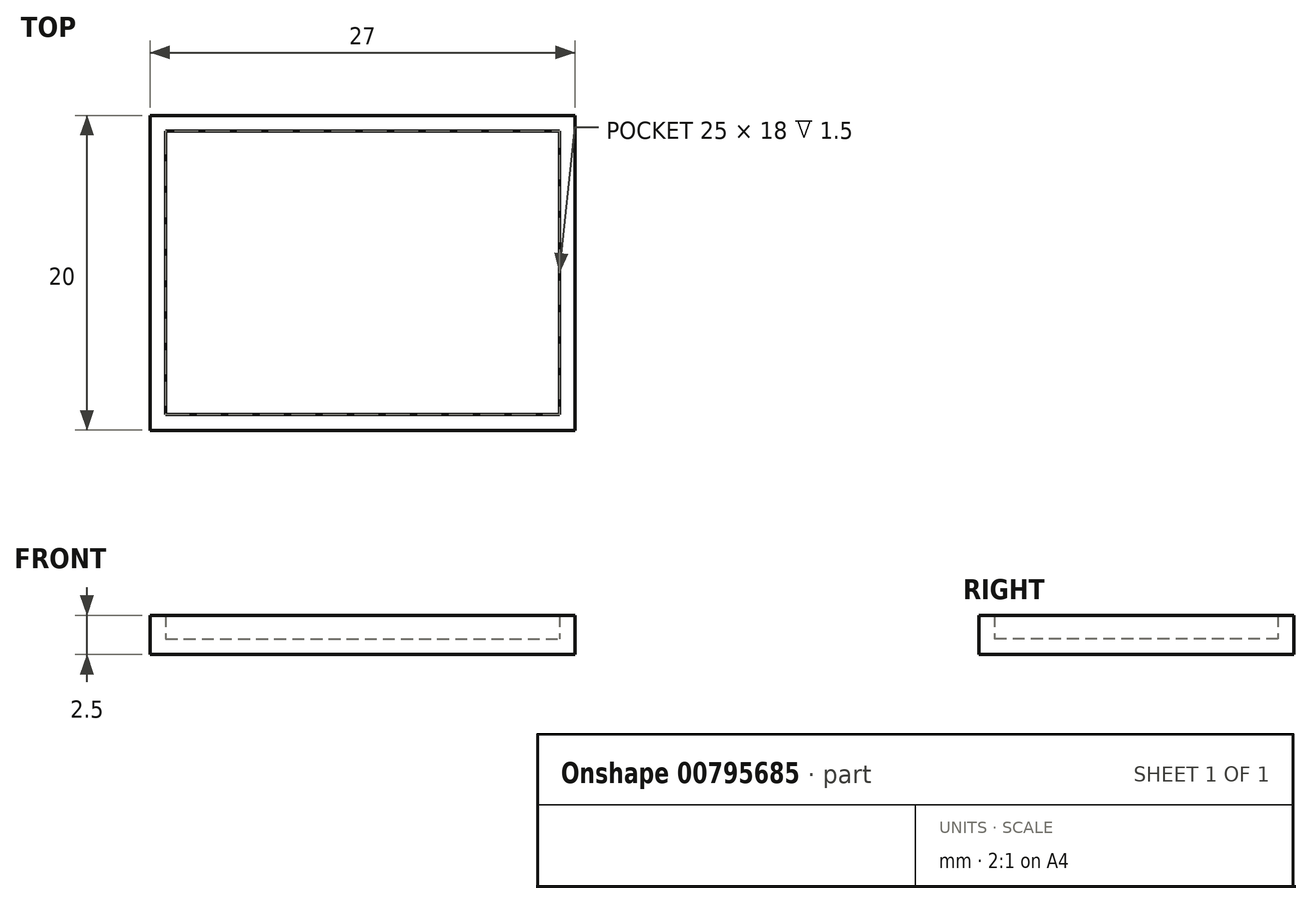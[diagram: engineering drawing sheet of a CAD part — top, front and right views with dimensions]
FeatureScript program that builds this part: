
annotation { "Feature Type Name" : "Feature", "Feature Type Description" : "" }
export const myFeature = defineFeature(function(context is Context, id is Id, definition is map)
    precondition{}
    {
        {
            var Q0;
            Q0=qCreatedBy(makeId("Top.planeOp"),FACE);
            var sketch = newSketch(context, id + "F0", { "sketchPlane" : qUnion([Q0])});
            skLineSegment(sketch, "E0.bottom", {"start": v(-48.16, 20.25) * mm, "end": v(-23.16, 20.25) * mm});
            skLineSegment(sketch, "E0.top", {"start": v(-48.16, 2.25) * mm, "end": v(-23.16, 2.25) * mm});
            skLineSegment(sketch, "E0.left", {"start": v(-48.16, 20.25) * mm, "end": v(-48.16, 2.25) * mm});
            skLineSegment(sketch, "E0.right", {"start": v(-23.16, 20.25) * mm, "end": v(-23.16, 2.25) * mm});
            skLineSegment(sketch, "E1.0", {"start": v(-49.16, 21.25) * mm, "end": v(-22.16, 21.25) * mm});
            skLineSegment(sketch, "E1.1", {"start": v(-49.16, 21.25) * mm, "end": v(-49.16, 1.25) * mm});
            skLineSegment(sketch, "E1.2", {"start": v(-49.16, 1.25) * mm, "end": v(-22.16, 1.25) * mm});
            skLineSegment(sketch, "E1.3", {"start": v(-22.16, 21.25) * mm, "end": v(-22.16, 1.25) * mm});
            skLineSegment(sketch, "E2", {"start": v(-23.16, 20.25) * mm, "end": v(-22.16, 20.25) * mm});
            skLineSegment(sketch, "E3", {"start": v(-23.16, 2.25) * mm, "end": v(-22.16, 2.25) * mm});
            skLineSegment(sketch, "E4", {"start": v(-48.16, 2.25) * mm, "end": v(-49.16, 2.25) * mm});
            skLineSegment(sketch, "E5", {"start": v(-48.16, 20.25) * mm, "end": v(-49.16, 20.25) * mm});
            skSolve(sketch);
        }
        {
            var Q0;
            Q0=makeQuery(id+"F0.imprint","IMPRINT",FACE,{"disambiguationData":[TD([[makeQuery(id+"F0.imprint","IMPRINT",EDGE,{"derivedFrom":sQuery(id+"F0.wireOp",EDGE,"E0.bottom")}),-1.0]])]});
            extrude(context, id + "F1", {"entities" : qUnion([Q0]), "depth" : 1 * mm, "offsetDistance" : 25 * mm});
        }
        {
            var Q0;
            Q0=makeQuery(id+"F0.imprint","IMPRINT",FACE,{"disambiguationData":[TD([[makeQuery(id+"F0.imprint","IMPRINT",EDGE,{"derivedFrom":sQuery(id+"F0.wireOp",EDGE,"E0.bottom")}),1.0]])]});
            var Q1;
            Q1=makeQuery(id+"F0.imprint","IMPRINT",FACE,{"disambiguationData":[TD([[makeQuery(id+"F0.imprint","IMPRINT",EDGE,{"derivedFrom":sQuery(id+"F0.wireOp",EDGE,"E0.top")}),-1.0]])]});
            var Q2;
            Q2=makeQuery(id+"F0.imprint","IMPRINT",FACE,{"disambiguationData":[TD([[makeQuery(id+"F0.imprint","IMPRINT",EDGE,{"derivedFrom":sQuery(id+"F0.wireOp",EDGE,"E0.left")}),-1.0]])]});
            var Q3;
            Q3=makeQuery(id+"F0.imprint","IMPRINT",FACE,{"disambiguationData":[TD([[makeQuery(id+"F0.imprint","IMPRINT",EDGE,{"derivedFrom":sQuery(id+"F0.wireOp",EDGE,"E0.right")}),1.0]])]});
            extrude(context, id + "F2", {"entities" : qUnion([Q0, Q1, Q2, Q3]), "operationType" : NewBodyOperationType.ADD, "depth" : 2.5 * mm, "offsetDistance" : 25 * mm});
        }
    });
